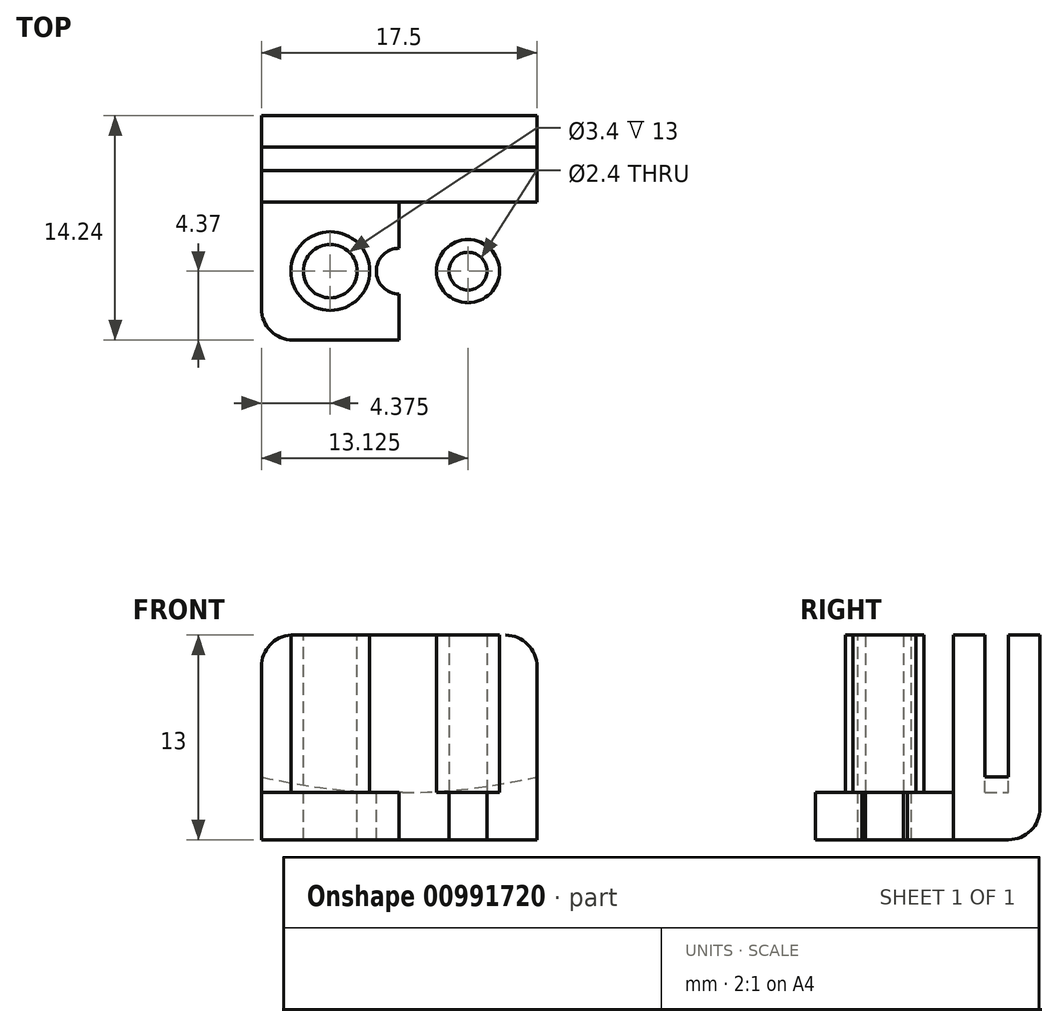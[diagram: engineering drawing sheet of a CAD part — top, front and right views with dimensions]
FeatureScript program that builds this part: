
annotation { "Feature Type Name" : "Feature", "Feature Type Description" : "" }
export const myFeature = defineFeature(function(context is Context, id is Id, definition is map)
    precondition{}
    {
        {
            var Q0;
            Q0=qCreatedBy(makeId("Top.planeOp"),FACE);
            var sketch = newSketch(context, id + "F0", { "sketchPlane" : qUnion([Q0])});
            skLineSegment(sketch, "E0", {"start": v(0, 0) * mm, "end": v(0, 7.12) * mm});
            skLineSegment(sketch, "E1", {"start": v(0, 7.12) * mm, "end": v(-8.75, 7.12) * mm});
            skLineSegment(sketch, "E2", {"start": v(-8.75, 7.12) * mm, "end": v(-8.75, 0) * mm});
            skLineSegment(sketch, "E3.MirrorCS", {"start": v(0, 7.12) * mm, "end": v(8.75, 7.12) * mm});
            skLineSegment(sketch, "E4.MirrorCS", {"start": v(8.75, 7.12) * mm, "end": v(8.75, 0) * mm});
            skLineSegment(sketch, "E5.MirrorCS", {"start": v(-8.75, -7.12) * mm, "end": v(-8.75, 0) * mm});
            skLineSegment(sketch, "E6.MirrorCS", {"start": v(0, -7.12) * mm, "end": v(-8.75, -7.12) * mm});
            skLineSegment(sketch, "E7.MirrorCS", {"start": v(0, -7.12) * mm, "end": v(8.75, -7.12) * mm});
            skLineSegment(sketch, "E8.MirrorCS", {"start": v(8.75, -7.12) * mm, "end": v(8.75, 0) * mm});
            skSolve(sketch);
        }
        {
            var Q0;
            Q0=makeQuery(id+"F0.imprint","IMPRINT",FACE,{"disambiguationData":[TD([[makeQuery(id+"F0.imprint","IMPRINT",EDGE,{"derivedFrom":sQuery(id+"F0.wireOp",EDGE,"E1")}),1.0]])]});
            extrude(context, id + "F1", {"entities" : qUnion([Q0]), "depth" : 3 * mm, "offsetDistance" : 25 * mm});
        }
        {
            var Q0;
            Q0=makeQuery(id+"F1.opExtrude","SWEPT_EDGE",EDGE,{"disambiguationData":[OSD([sQuery(id+"F0.wireOp",EDGE,"E5.MirrorCS"),sQuery(id+"F0.wireOp",EDGE,"E6.MirrorCS")])]});
            var Q1;
            Q1=makeQuery(id+"F1.opExtrude","SWEPT_EDGE",EDGE,{"disambiguationData":[OSD([sQuery(id+"F0.wireOp",EDGE,"E7.MirrorCS"),sQuery(id+"F0.wireOp",EDGE,"E8.MirrorCS")])]});
            fillet(context, id + "F2", {"entities" : qUnion([Q0, Q1]), "radius" : 2 * mm, "tangentPropagation" : true, "allowEdgeOverflow" : false});
        }
        {
            var Q0;
            Q0=makeQuery(id+"F1.opExtrude","CAP_FACE",FACE,{"disambiguationData":[OSD([sQuery(id+"F0.wireOp",EDGE,"E1"),sQuery(id+"F0.wireOp",EDGE,"E2"),sQuery(id+"F0.wireOp",EDGE,"E3.MirrorCS"),sQuery(id+"F0.wireOp",EDGE,"E4.MirrorCS"),sQuery(id+"F0.wireOp",EDGE,"E5.MirrorCS"),sQuery(id+"F0.wireOp",EDGE,"E6.MirrorCS"),sQuery(id+"F0.wireOp",EDGE,"E7.MirrorCS"),sQuery(id+"F0.wireOp",EDGE,"E8.MirrorCS")])],"isStart":false});
            var sketch = newSketch(context, id + "F3", { "sketchPlane" : qUnion([Q0])});
            skLineSegment(sketch, "E9", {"start": v(-8.75, 7.12) * mm, "end": v(8.75, 7.12) * mm});
            skLineSegment(sketch, "E10", {"start": v(8.75, 7.12) * mm, "end": v(8.75, 5.13) * mm});
            skLineSegment(sketch, "E11", {"start": v(8.75, 5.13) * mm, "end": v(-8.75, 5.13) * mm});
            skLineSegment(sketch, "E12", {"start": v(-8.75, 5.13) * mm, "end": v(-8.75, 7.12) * mm});
            skSolve(sketch);
        }
        {
            var Q0;
            Q0=makeQuery(id+"F3.imprint","IMPRINT",FACE,{"disambiguationData":[TD([[makeQuery(id+"F3.imprint","IMPRINT",EDGE,{"derivedFrom":sQuery(id+"F3.wireOp",EDGE,"E9")}),-1.0]])]});
            extrude(context, id + "F4", {"entities" : qUnion([Q0]), "operationType" : NewBodyOperationType.ADD, "depth" : 10 * mm, "offsetDistance" : 25 * mm});
        }
        {
            var Q0;
            Q0=makeQuery(id+"F1.opExtrude","CAP_FACE",FACE,{"disambiguationData":[OSD([sQuery(id+"F0.wireOp",EDGE,"E1"),sQuery(id+"F0.wireOp",EDGE,"E2"),sQuery(id+"F0.wireOp",EDGE,"E3.MirrorCS"),sQuery(id+"F0.wireOp",EDGE,"E4.MirrorCS"),sQuery(id+"F0.wireOp",EDGE,"E5.MirrorCS"),sQuery(id+"F0.wireOp",EDGE,"E6.MirrorCS"),sQuery(id+"F0.wireOp",EDGE,"E7.MirrorCS"),sQuery(id+"F0.wireOp",EDGE,"E8.MirrorCS")])],"isStart":false});
            var sketch = newSketch(context, id + "F5", { "sketchPlane" : qUnion([Q0])});
            skLineSegment(sketch, "E13", {"start": v(0, 5.13) * mm, "end": v(0, 3.63) * mm});
            skLineSegment(sketch, "E14", {"start": v(0, 3.63) * mm, "end": v(-8.75, 3.63) * mm});
            skLineSegment(sketch, "E15", {"start": v(-8.75, 3.63) * mm, "end": v(-8.75, 1.63) * mm});
            skLineSegment(sketch, "E16", {"start": v(-8.75, 1.63) * mm, "end": v(8.75, 1.63) * mm});
            skLineSegment(sketch, "E17", {"start": v(8.75, 1.63) * mm, "end": v(8.75, 3.63) * mm});
            skLineSegment(sketch, "E18", {"start": v(8.75, 3.63) * mm, "end": v(0, 3.63) * mm});
            skSolve(sketch);
        }
        {
            var Q0;
            Q0=makeQuery(id+"F5.imprint","IMPRINT",FACE,{"disambiguationData":[TD([[makeQuery(id+"F5.imprint","IMPRINT",EDGE,{"derivedFrom":sQuery(id+"F5.wireOp",EDGE,"E14")}),1.0]])]});
            extrude(context, id + "F6", {"entities" : qUnion([Q0]), "operationType" : NewBodyOperationType.ADD, "depth" : 10 * mm, "offsetDistance" : 25 * mm});
        }
        {
            var Q0;
            Q0=makeQuery(id+"F6.opExtrude","CAP_EDGE",EDGE,{"disambiguationData":[OSD([sQuery(id+"F5.wireOp",EDGE,"E15")])],"isStart":false});
            var Q1;
            Q1=makeQuery(id+"F6.opExtrude","CAP_EDGE",EDGE,{"disambiguationData":[OSD([sQuery(id+"F5.wireOp",EDGE,"E17")])],"isStart":false});
            var Q2;
            Q2=makeQuery(id+"F4.opExtrude","CAP_EDGE",EDGE,{"disambiguationData":[OSD([sQuery(id+"F3.wireOp",EDGE,"E12")])],"isStart":false});
            var Q3;
            Q3=makeQuery(id+"F4.opExtrude","CAP_EDGE",EDGE,{"disambiguationData":[OSD([sQuery(id+"F3.wireOp",EDGE,"E10")])],"isStart":false});
            fillet(context, id + "F7", {"entities" : qUnion([Q0, Q1, Q2, Q3]), "radius" : 2 * mm, "tangentPropagation" : true, "allowEdgeOverflow" : false});
        }
        {
            var Q0;
            {var subQ0=sQuery(id+"F0.wireOp",EDGE,"E6.MirrorCS");var subQ1=sQuery(id+"F0.wireOp",EDGE,"E5.MirrorCS");var subQ2=sQuery(id+"F0.wireOp",EDGE,"E8.MirrorCS");var subQ3=sQuery(id+"F0.wireOp",EDGE,"E4.MirrorCS");var subQ4=sQuery(id+"F0.wireOp",EDGE,"E7.MirrorCS");var subQ5=sQuery(id+"F0.wireOp",EDGE,"E2");Q0=makeQuery(id+"F6.boolean.opBoolean","SPLIT",FACE,{"disambiguationData":[TD([makeQuery(id+"F6.opExtrude","SWEPT_FACE",FACE,{"disambiguationData":[OSD([sQuery(id+"F5.wireOp",EDGE,"E16")])]})])],"derivedFrom":makeQuery(id+"F1.opExtrude","CAP_FACE",FACE,{"disambiguationData":[OSD([sQuery(id+"F0.wireOp",EDGE,"E1"),subQ5,sQuery(id+"F0.wireOp",EDGE,"E3.MirrorCS"),subQ3,subQ1,subQ0,subQ4,subQ2])],"isStart":false})});}
            var sketch = newSketch(context, id + "F8", { "sketchPlane" : qUnion([Q0])});
            skLineSegment(sketch, "E19", {"start": v(0, 1.63) * mm, "end": v(0, -7.12) * mm});
            skLineSegment(sketch, "E20", {"start": v(0, -2.75) * mm, "end": v(-8.75, -2.75) * mm});
            skLineSegment(sketch, "E21", {"start": v(0, -2.75) * mm, "end": v(8.75, -2.75) * mm});
            skCircle(sketch, "E22", {"center": v(0, -2.75) * mm, "radius": 1.45 * mm});
            skCircle(sketch, "E23", {"center": v(-4.38, -2.75) * mm, "radius": 1.7 * mm});
            skCircle(sketch, "E24", {"center": v(4.38, -2.75) * mm, "radius": 1.2 * mm});
            skSolve(sketch);
        }
        {
            var Q0;
            {var subQ0=sQuery(id+"F8.wireOp",EDGE,"E23");var subQ1=sQuery(id+"F8.wireOp",EDGE,"E20");var subQ2=makeQuery(id+"F8.imprint","INTERSECT",VERTEX,{"disambiguationData":[OD(0.0)],"derivedFrom":[subQ1,subQ0]});Q0=makeQuery(id+"F8.imprint","IMPRINT",FACE,{"disambiguationData":[TD([[makeQuery(id+"F8.imprint","IMPRINT",EDGE,{"disambiguationData":[TD([[subQ2,-1.0]])],"derivedFrom":subQ1}),-1.0]])]});}
            var Q1;
            {var subQ0=sQuery(id+"F8.wireOp",EDGE,"E23");var subQ1=sQuery(id+"F8.wireOp",EDGE,"E20");var subQ2=makeQuery(id+"F8.imprint","INTERSECT",VERTEX,{"disambiguationData":[OD(0.0)],"derivedFrom":[subQ1,subQ0]});Q1=makeQuery(id+"F8.imprint","IMPRINT",FACE,{"disambiguationData":[TD([[makeQuery(id+"F8.imprint","IMPRINT",EDGE,{"disambiguationData":[TD([[subQ2,-1.0]])],"derivedFrom":subQ1}),1.0]])]});}
            var Q2;
            {var subQ1=sQuery(id+"F8.wireOp",EDGE,"E19");var subQ3=sQuery(id+"F8.wireOp",EDGE,"E22");var subQ4=makeQuery(id+"F8.imprint","INTERSECT",VERTEX,{"disambiguationData":[OD(0.0)],"derivedFrom":[subQ1,subQ3]});Q2=makeQuery(id+"F8.imprint","IMPRINT",FACE,{"disambiguationData":[TD([[makeQuery(id+"F8.imprint","IMPRINT",EDGE,{"disambiguationData":[TD([[subQ4,-1.0]])],"derivedFrom":subQ3}),1.0]])]});}
            var Q3;
            {var subQ1=sQuery(id+"F8.wireOp",EDGE,"E19");var subQ3=sQuery(id+"F8.wireOp",EDGE,"E22");var subQ4=makeQuery(id+"F8.imprint","INTERSECT",VERTEX,{"disambiguationData":[OD(1.0)],"derivedFrom":[subQ1,subQ3]});Q3=makeQuery(id+"F8.imprint","IMPRINT",FACE,{"disambiguationData":[TD([[makeQuery(id+"F8.imprint","IMPRINT",EDGE,{"disambiguationData":[TD([[subQ4,1.0]])],"derivedFrom":subQ3}),1.0]])]});}
            var Q4;
            {var subQ1=sQuery(id+"F8.wireOp",EDGE,"E19");var subQ3=sQuery(id+"F8.wireOp",EDGE,"E22");var subQ4=makeQuery(id+"F8.imprint","INTERSECT",VERTEX,{"disambiguationData":[OD(1.0)],"derivedFrom":[subQ1,subQ3]});Q4=makeQuery(id+"F8.imprint","IMPRINT",FACE,{"disambiguationData":[TD([[makeQuery(id+"F8.imprint","IMPRINT",EDGE,{"disambiguationData":[TD([[subQ4,-1.0]])],"derivedFrom":subQ3}),1.0]])]});}
            var Q5;
            {var subQ1=sQuery(id+"F8.wireOp",EDGE,"E19");var subQ3=sQuery(id+"F8.wireOp",EDGE,"E22");var subQ4=makeQuery(id+"F8.imprint","INTERSECT",VERTEX,{"disambiguationData":[OD(0.0)],"derivedFrom":[subQ1,subQ3]});Q5=makeQuery(id+"F8.imprint","IMPRINT",FACE,{"disambiguationData":[TD([[makeQuery(id+"F8.imprint","IMPRINT",EDGE,{"disambiguationData":[TD([[subQ4,1.0]])],"derivedFrom":subQ3}),1.0]])]});}
            var Q6;
            {var subQ0=sQuery(id+"F8.wireOp",EDGE,"E24");var subQ1=sQuery(id+"F8.wireOp",EDGE,"E21");var subQ2=makeQuery(id+"F8.imprint","INTERSECT",VERTEX,{"disambiguationData":[OD(0.0)],"derivedFrom":[subQ1,subQ0]});Q6=makeQuery(id+"F8.imprint","IMPRINT",FACE,{"disambiguationData":[TD([[makeQuery(id+"F8.imprint","IMPRINT",EDGE,{"disambiguationData":[TD([[subQ2,-1.0]])],"derivedFrom":subQ1}),1.0]])]});}
            var Q7;
            {var subQ0=sQuery(id+"F8.wireOp",EDGE,"E24");var subQ1=sQuery(id+"F8.wireOp",EDGE,"E21");var subQ2=makeQuery(id+"F8.imprint","INTERSECT",VERTEX,{"disambiguationData":[OD(0.0)],"derivedFrom":[subQ1,subQ0]});Q7=makeQuery(id+"F8.imprint","IMPRINT",FACE,{"disambiguationData":[TD([[makeQuery(id+"F8.imprint","IMPRINT",EDGE,{"disambiguationData":[TD([[subQ2,-1.0]])],"derivedFrom":subQ1}),-1.0]])]});}
            var Q8;
            Q8=makeQuery(id+"F1.opExtrude","CAP_FACE",FACE,{"disambiguationData":[OSD([sQuery(id+"F0.wireOp",EDGE,"E1"),sQuery(id+"F0.wireOp",EDGE,"E2"),sQuery(id+"F0.wireOp",EDGE,"E3.MirrorCS"),sQuery(id+"F0.wireOp",EDGE,"E4.MirrorCS"),sQuery(id+"F0.wireOp",EDGE,"E5.MirrorCS"),sQuery(id+"F0.wireOp",EDGE,"E6.MirrorCS"),sQuery(id+"F0.wireOp",EDGE,"E7.MirrorCS"),sQuery(id+"F0.wireOp",EDGE,"E8.MirrorCS")])],"isStart":true});
            extrude(context, id + "F9", {"entities" : qUnion([Q0, Q1, Q2, Q3, Q4, Q5, Q6, Q7]), "operationType" : NewBodyOperationType.REMOVE, "endBound" : BoundingType.UP_TO_SURFACE, "oppositeDirection" : true, "depth" : 25 * mm, "endBoundEntityFace" : qUnion([Q8]), "offsetDistance" : 25 * mm});
        }
        {
            var Q0;
            Q0=makeQuery(id+"F4.opExtrude","SWEPT_FACE",FACE,{"disambiguationData":[OSD([sQuery(id+"F3.wireOp",EDGE,"E11")])]});
            var sketch = newSketch(context, id + "F10", { "sketchPlane" : qUnion([Q0])});
            skLineSegment(sketch, "E25", {"start": v(-8.75, 3) * mm, "end": v(-8.75, 4) * mm});
            skLineSegment(sketch, "E26.MirrorCS", {"start": v(8.75, 3) * mm, "end": v(8.75, 4) * mm});
            skArc(sketch, "E27", {"start": v(-8.75, 4) * mm, "mid": v(-4.4, 3.25) * mm, "end": v(0, 3) * mm});
            skArc(sketch, "E28.MirrorCS", {"start": v(8.75, 4) * mm, "mid": v(4.4, 3.25) * mm, "end": v(0, 3) * mm});
            skSolve(sketch);
        }
        {
            var Q0;
            {var subQ0=sQuery(id+"F10.wireOp",EDGE,"E26.MirrorCS");Q0=makeQuery(id+"F10.imprint","IMPRINT",FACE,{"disambiguationData":[TD([[makeQuery(id+"F10.imprint","IMPRINT",EDGE,{"derivedFrom":subQ0}),-1.0]])]});}
            var Q1;
            {var subQ0=sQuery(id+"F10.wireOp",EDGE,"E25");Q1=makeQuery(id+"F10.imprint","IMPRINT",FACE,{"disambiguationData":[TD([[makeQuery(id+"F10.imprint","IMPRINT",EDGE,{"derivedFrom":subQ0}),1.0]])]});}
            var Q2;
            Q2=makeQuery(id+"F6.opExtrude","SWEPT_FACE",FACE,{"disambiguationData":[OSD([sQuery(id+"F5.wireOp",EDGE,"E14"),sQuery(id+"F5.wireOp",EDGE,"E18")])]});
            extrude(context, id + "F11", {"entities" : qUnion([Q0, Q1]), "operationType" : NewBodyOperationType.ADD, "endBound" : BoundingType.UP_TO_SURFACE, "depth" : 25 * mm, "endBoundEntityFace" : qUnion([Q2]), "offsetDistance" : 25 * mm});
        }
        {
            var Q0;
            Q0=makeQuery(id+"F1.opExtrude","CAP_EDGE",EDGE,{"disambiguationData":[OSD([sQuery(id+"F0.wireOp",EDGE,"E1"),sQuery(id+"F0.wireOp",EDGE,"E3.MirrorCS")])],"isStart":true});
            var Q1;
            Q1=makeQuery(id+"F6.opExtrude","CAP_EDGE",EDGE,{"disambiguationData":[OSD([sQuery(id+"F5.wireOp",EDGE,"E16")])],"isStart":true});
            fillet(context, id + "F12", {"entities" : qUnion([Q0, Q1]), "radius" : 2 * mm, "tangentPropagation" : true, "allowEdgeOverflow" : false});
        }
        {
            var Q0;
            {var subQ0=sQuery(id+"F0.wireOp",EDGE,"E6.MirrorCS");var subQ1=sQuery(id+"F0.wireOp",EDGE,"E5.MirrorCS");var subQ2=sQuery(id+"F0.wireOp",EDGE,"E8.MirrorCS");var subQ3=sQuery(id+"F0.wireOp",EDGE,"E4.MirrorCS");var subQ4=sQuery(id+"F0.wireOp",EDGE,"E7.MirrorCS");var subQ5=sQuery(id+"F0.wireOp",EDGE,"E2");Q0=makeQuery(id+"F6.boolean.opBoolean","SPLIT",FACE,{"disambiguationData":[TD([makeQuery(id+"F6.opExtrude","SWEPT_FACE",FACE,{"disambiguationData":[OSD([sQuery(id+"F5.wireOp",EDGE,"E16")])]})])],"derivedFrom":makeQuery(id+"F1.opExtrude","CAP_FACE",FACE,{"disambiguationData":[OSD([sQuery(id+"F0.wireOp",EDGE,"E1"),subQ5,sQuery(id+"F0.wireOp",EDGE,"E3.MirrorCS"),subQ3,subQ1,subQ0,subQ4,subQ2])],"isStart":false})});}
            var sketch = newSketch(context, id + "F13", { "sketchPlane" : qUnion([Q0])});
            skCircle(sketch, "E29.0", {"center": v(-4.38, -2.75) * mm, "radius": 2.5 * mm});
            skCircle(sketch, "E30.0", {"center": v(0, -2.75) * mm, "radius": 2.25 * mm});
            skCircle(sketch, "E31.0", {"center": v(4.38, -2.75) * mm, "radius": 2 * mm});
            skSolve(sketch);
        }
        {
            var Q0;
            Q0=makeQuery(id+"F13.imprint","IMPRINT",FACE,{"disambiguationData":[TD([[makeQuery(id+"F13.imprint","IMPRINT",EDGE,{"derivedFrom":makeQuery(id+"F9.boolean.opBoolean","COPY",EDGE,{"derivedFrom":makeQuery(id+"F9.opExtrude","CAP_EDGE",EDGE,{"disambiguationData":[OSD([sQuery(id+"F8.wireOp",EDGE,"E22")])],"isStart":true})})}),1.0]])]});
            var Q1;
            Q1=makeQuery(id+"F13.imprint","IMPRINT",FACE,{"disambiguationData":[TD([[makeQuery(id+"F13.imprint","IMPRINT",EDGE,{"derivedFrom":makeQuery(id+"F9.boolean.opBoolean","COPY",EDGE,{"derivedFrom":makeQuery(id+"F9.opExtrude","CAP_EDGE",EDGE,{"disambiguationData":[OSD([sQuery(id+"F8.wireOp",EDGE,"E23")])],"isStart":true})})}),1.0]])]});
            var Q2;
            Q2=makeQuery(id+"F13.imprint","IMPRINT",FACE,{"disambiguationData":[TD([[makeQuery(id+"F13.imprint","IMPRINT",EDGE,{"derivedFrom":makeQuery(id+"F9.boolean.opBoolean","COPY",EDGE,{"derivedFrom":makeQuery(id+"F9.opExtrude","CAP_EDGE",EDGE,{"disambiguationData":[OSD([sQuery(id+"F8.wireOp",EDGE,"E24")])],"isStart":true})})}),1.0]])]});
            var Q3;
            {var subQ0=sQuery(id+"F13.wireOp",EDGE,"E30.0");var subQ1=sQuery(id+"F13.wireOp",EDGE,"E29.0");var subQ2=makeQuery(id+"F13.imprint","INTERSECT",VERTEX,{"disambiguationData":[OD(0.0)],"derivedFrom":[subQ1,subQ0]});Q3=makeQuery(id+"F13.imprint","IMPRINT",FACE,{"disambiguationData":[TD([[makeQuery(id+"F13.imprint","IMPRINT",EDGE,{"disambiguationData":[TD([[subQ2,1.0]])],"derivedFrom":subQ1}),1.0]])]});}
            var Q4;
            Q4=makeQuery(id+"F13.imprint","IMPRINT",FACE,{"disambiguationData":[TD([[makeQuery(id+"F13.imprint","IMPRINT",EDGE,{"derivedFrom":sQuery(id+"F13.wireOp",EDGE,"E31.0")}),1.0]])]});
            var Q5;
            Q5=makeQuery(id+"F13.imprint","IMPRINT",FACE,{"disambiguationData":[TD([[makeQuery(id+"F13.imprint","IMPRINT",EDGE,{"derivedFrom":makeQuery(id+"F9.boolean.opBoolean","COPY",EDGE,{"derivedFrom":makeQuery(id+"F9.opExtrude","CAP_EDGE",EDGE,{"disambiguationData":[OSD([sQuery(id+"F8.wireOp",EDGE,"E22")])],"isStart":true})})}),-1.0]])]});
            var Q6;
            {var subQ0=sQuery(id+"F13.wireOp",EDGE,"E29.0");var subQ1=sQuery(id+"F0.wireOp",EDGE,"E6.MirrorCS");var subQ2=sQuery(id+"F0.wireOp",EDGE,"E5.MirrorCS");var subQ3=sQuery(id+"F0.wireOp",EDGE,"E8.MirrorCS");var subQ4=sQuery(id+"F0.wireOp",EDGE,"E4.MirrorCS");var subQ5=sQuery(id+"F0.wireOp",EDGE,"E7.MirrorCS");var subQ6=sQuery(id+"F0.wireOp",EDGE,"E2");var subQ7=sQuery(id+"F5.wireOp",EDGE,"E16");var subQ8=makeQuery(id+"F12.opFillet","BLEND_EDGE",EDGE,{"blendedFrom":[makeQuery(id+"F6.opExtrude","CAP_EDGE",EDGE,{"disambiguationData":[OSD([subQ7])],"isStart":true}),makeQuery(id+"F6.boolean.opBoolean","SPLIT",FACE,{"disambiguationData":[TD([makeQuery(id+"F6.opExtrude","SWEPT_FACE",FACE,{"disambiguationData":[OSD([subQ7])]})])],"derivedFrom":makeQuery(id+"F1.opExtrude","CAP_FACE",FACE,{"disambiguationData":[OSD([sQuery(id+"F0.wireOp",EDGE,"E1"),subQ6,sQuery(id+"F0.wireOp",EDGE,"E3.MirrorCS"),subQ4,subQ2,subQ1,subQ5,subQ3])],"isStart":false})})],"blendedInto":[makeQuery(id+"F6.boolean.opBoolean","SPLIT",FACE,{"disambiguationData":[TD([makeQuery(id+"F6.opExtrude","SWEPT_FACE",FACE,{"disambiguationData":[OSD([subQ7])]})])],"derivedFrom":makeQuery(id+"F1.opExtrude","CAP_FACE",FACE,{"disambiguationData":[OSD([sQuery(id+"F0.wireOp",EDGE,"E1"),subQ6,sQuery(id+"F0.wireOp",EDGE,"E3.MirrorCS"),subQ4,subQ2,subQ1,subQ5,subQ3])],"isStart":false})})]});var subQ9=makeQuery(id+"F13.imprint","INTERSECT",VERTEX,{"disambiguationData":[OD(0.0)],"derivedFrom":[subQ8,subQ0]});Q6=makeQuery(id+"F13.imprint","IMPRINT",FACE,{"disambiguationData":[TD([[makeQuery(id+"F13.imprint","IMPRINT",EDGE,{"disambiguationData":[TD([[subQ9,-1.0]])],"derivedFrom":subQ0}),1.0]])]});}
            var Q7;
            Q7=makeQuery(id+"F13.imprint","IMPRINT",FACE,{"disambiguationData":[TD([[makeQuery(id+"F13.imprint","IMPRINT",EDGE,{"derivedFrom":makeQuery(id+"F9.boolean.opBoolean","COPY",EDGE,{"derivedFrom":makeQuery(id+"F9.opExtrude","CAP_EDGE",EDGE,{"disambiguationData":[OSD([sQuery(id+"F8.wireOp",EDGE,"E23")])],"isStart":true})})}),-1.0]])]});
            var Q8;
            Q8=makeQuery(id+"F6.opExtrude","CAP_FACE",FACE,{"disambiguationData":[OSD([sQuery(id+"F5.wireOp",EDGE,"E14"),sQuery(id+"F5.wireOp",EDGE,"E15"),sQuery(id+"F5.wireOp",EDGE,"E16"),sQuery(id+"F5.wireOp",EDGE,"E17"),sQuery(id+"F5.wireOp",EDGE,"E18")])],"isStart":false});
            extrude(context, id + "F14", {"entities" : qUnion([Q0, Q1, Q2, Q3, Q4, Q5, Q6, Q7]), "operationType" : NewBodyOperationType.ADD, "endBound" : BoundingType.UP_TO_SURFACE, "depth" : 5 * mm, "endBoundEntityFace" : qUnion([Q8]), "offsetDistance" : 25 * mm});
        }
        {
            var Q0;
            Q0 = qSketchRegion(id + "F8", true);
            var Q1;
            Q1=makeQuery(id+"F6.opExtrude","CAP_FACE",FACE,{"disambiguationData":[OSD([sQuery(id+"F5.wireOp",EDGE,"E14"),sQuery(id+"F5.wireOp",EDGE,"E15"),sQuery(id+"F5.wireOp",EDGE,"E16"),sQuery(id+"F5.wireOp",EDGE,"E17"),sQuery(id+"F5.wireOp",EDGE,"E18")])],"isStart":false});
            extrude(context, id + "F15", {"entities" : qUnion([Q0]), "operationType" : NewBodyOperationType.REMOVE, "endBound" : BoundingType.UP_TO_SURFACE, "depth" : 25 * mm, "endBoundEntityFace" : qUnion([Q1]), "offsetDistance" : 25 * mm});
        }
    });
